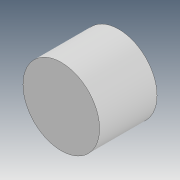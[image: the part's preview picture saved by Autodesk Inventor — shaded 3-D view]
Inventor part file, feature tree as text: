
AUTODESK INVENTOR PART (.ipt)
format: ipt  version: 2021 (Build 250183000, 183)  size: 78,336 bytes
history: native  units: in
note: dims shown in document units (in); Inventor stores cm internally (conversion verified against a paired STEP export)
features: sketch x2, other x1, extrude x1
ambient origin geometry x8: Origin, YZ Plane, XZ Plane, XY Plane, X Axis, Y Axis, Z Axis, Center Point
bodies: Body1 (feature_tree)
feature tree (4):
  other  "Sólido1"
  sketch  "Esboço1"  dims[d0=0.0787in d1=0.0591in d2=0.0in]
  extrude  "Extrusão1"  Depth=0.0591in TaperAngle=0.0deg
  sketch  "Esboço2"
